# Revit family: ONHPH
name_source: partatom
category: Mechanical Equipment
units: mm (PartAtom-declared; Revit-internal decimal feet)

## family parameters
Always vertical = Yes
Cut with Voids When Loaded = No
OmniClass Number = 23.40.40.11.17
OmniClass Title = Refrigerated Cases
Part Type = Normal
Room Calculation Point = No
Round Connector Dimension = Use Radius
Shared = No
Work Plane-Based = Yes

## types (12) — shared parameters
12" Shelf = Yes
14" Shelf = Yes
16" Shelf = Yes
18" Shelf = Yes
20" Shelf = Yes
BOTTOM ELECTRICAL = Yes
BOTTOM REFRIGERATION PIPING = Yes
Certifications = NSF 7, UL471, CSA
DATE = 05/23/2016
DESIGNERS NAME = SHIDDRAMESH
DRAIN PIPING = Yes
Default Elevation = 48"
Defrosts Per Day = 3
Description = High Narrow Multi-Deck Merchandiser
EQUIPMENT DESCRIPTION = High Narrow Multi-Deck Merchandiser
EQUIPMENT MARK = ONHPH
Electric Defrost Fail-Safe = 35 (Min)
Electric Defrost Termination Temp (°F) = 47 °F
GLASS = Glass
Height = 81"
Item Description = High Narrow Multi-Deck Merchandiser
LF STD END = Yes
Legend Number = ONHPH
Manufacturer = HILL PHOENIX
Model = ONHPH
PAINTED METAL UPPER SHELF = PAINTED SHELVES
REAR REFRIGERATION PIPING = Yes
REFRIGERATION PIPING = COPPER PIPE
RT STD END = Yes
Run-Off Time (Min) = 6-8 (Min)
STAINLESS STEEL = GALVANIZED STEEL
Standard Power Amps = 0 A
Superheat Set Point @ Bulb (°F) = 6-8 °F
TOP ELECTRICAL = Yes
TOP REFRIGERATION PIPING = Yes
Timed-Off Defrost Fail-Safe (Min) = 45 (Min)
Timed-Off Defrost Termination Temp = 47 °F
URL = http://www.hillphoenix.com
Width = 35 7/8"

## per-type parameters (varying)
| type | Application Discipline | BTUH Conventional | BTUH Parallel | CENTER LINE | Defrost (Phase 1) 208 V Amps | Defrost (Phase 1) 208 V Watts | Defrost (Phase 1) 240 V Amps | Defrost (Phase 1) 240 V Watts | Discharge Air (°F) | Discharge Air Velocity (FPM) | Evaporator (°F) | High Efficiency Amps | High Efficiency Watts | High Power (Cornice) Amps | High Power (Cornice) Watts | Length | Length of Cases | Light Length | Lights Per Row | Number of Fans | Refgn | Standard Power Watts |
| 04' Cut Produce | Cut Produce | 1305 | 1210 | 24" | 2 A | 400 W | 2 A | 532 W | 34 °F | 330 FPM | 26 °F | 0 A | 28 W | 0 A | 22 W | 48" | 48" | 4' | 1 | 2 | 7 5/8" | 12 W |
| 06' Cut Produce | Cut Produce | 1305 | 1210 | 36" | 3 A | 600 W | 3 A | 798 W | 34 °F | 330 FPM | 26 °F | 1 A | 42 W | 0 A | 30 W | 72" | 72" | 3' | 2 | 3 | 8 5/8" | 17 W |
| 08' Cut Produce | Cut Produce | 1305 | 1210 | 48" | 4 A | 800 W | 4 A | 1085 W | 34 °F | 330 FPM | 26 °F | 1 A | 56 W | 0 A | 43 W | 96" | 96" | 4' | 2 | 4 | 8 5/8" | 24 W |
| 12' Cut Produce | Cut Produce | 1305 | 1210 | 72" | 6 A | 1200 W | 7 A | 1600 W | 34 °F | 330 FPM | 26 °F | 1 A | 70 W | 1 A | 65 W | 144" | 144" | 4' | 3 | 5 | 8 5/8" | 36 W |
| 04' Bulk Produce | Bulk Produce | 890 | 825 | 24" | 2 A | 400 W | 2 A | 532 W | 37 °F | 230 FPM | 29 °F | 0 A | 28 W | 0 A | 22 W | 48" | 48" | 4' | 1 | 2 | 7 5/8" | 12 W |
| 06 'Bulk Produce | Bulk Produce | 890 | 825 | 36" | 3 A | 600 W | 3 A | 798 W | 37 °F | 230 FPM | 29 °F | 1 A | 42 W | 0 A | 30 W | 72" | 72" | 3' | 2 | 3 | 8 5/8" | 17 W |
| 08' Bulk Produce | Bulk Produce | 890 | 825 | 48" | 4 A | 800 W | 4 A | 1085 W | 37 °F | 230 FPM | 29 °F | 1 A | 56 W | 0 A | 43 W | 96" | 96" | 4' | 2 | 4 | 8 5/8" | 24 W |
| 12' Bulk Produce | Bulk Produce | 890 | 825 | 72" | 6 A | 1200 W | 7 A | 1600 W | 37 °F | 230 FPM | 29 °F | 1 A | 70 W | 1 A | 65 W | 144" | 144" | 4' | 3 | 5 | 8 5/8" | 36 W |
| 12' | Bulk Produce | 890 | 825 | 72" | 6 A | 1200 W | 7 A | 1600 W | 37 °F | 230 FPM | 29 °F | 1 A | 70 W | 0 A | 45 W | 144" | 48" | 4' | 3 | 5 | 8 5/8" | 18 W |
| 8' | Bulk Produce | 890 | 825 | 48" | 4 A | 800 W | 4 A | 1065 W | 37 °F | 230 FPM | 29 °F | 1 A | 56 W | 0 A | 30 W | 96" | 48" | 4' | 2 | 4 | 8 5/8" | 12 W |
| 6' | Bulk Produce | 890 | 825 | 36" | 3 A | 600 W | 3 A | 798 W | 37 °F | 230 FPM | 29 °F | 1 A | 42 W | 0 A | 24 W | 72" | 48" | 3' | 2 | 3 | 8 5/8" | 9 W |
| 4' | Cut Produce | 1305 | 1210 | 24" | 2 A | 400 W | 2 A | 532 W | 34 °F | 330 FPM | 26 °F | 0 A | 28 W | 0 A | 15 W | 48" | 48" | 4' | 1 | 2 | 7 5/8" | 6 W |

## geometry (parser evidence)
native form markers: Blend x12, Sweep x4
no freeform markers — native parametric forms only
